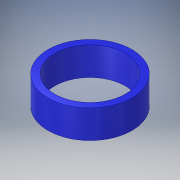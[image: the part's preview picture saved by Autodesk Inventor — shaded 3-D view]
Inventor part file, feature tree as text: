
AUTODESK INVENTOR PART (.ipt)
format: ipt  version: 2018 (Build 220112000, 112)  size: 117,760 bytes
history: native  units: in
note: dims shown in document units (in); Inventor stores cm internally (conversion verified against a paired STEP export)
features: revolve x1, sketch x1
ambient origin geometry x8: Origin, YZ Plane, XZ Plane, XY Plane, X Axis, Y Axis, Z Axis, Center Point
bodies: Solid1 (feature_tree)
feature tree (2):
  revolve  "Revolution1"  [1 undecoded]
  sketch  "Sketch1"  dims[d0=1.5625in d1=5.0in d3=14.0in d4=90.0deg d5=1.4844in d6=1.0in d7=2.5in d9=0.75in d10=0.25in d11=0.75in d12=0.2344in]
note: 1 required parameter value undecoded (feature->parameter linkage not recoverable at this tier; creation-order binding heuristic only, values carry confidence <= 0.55)
